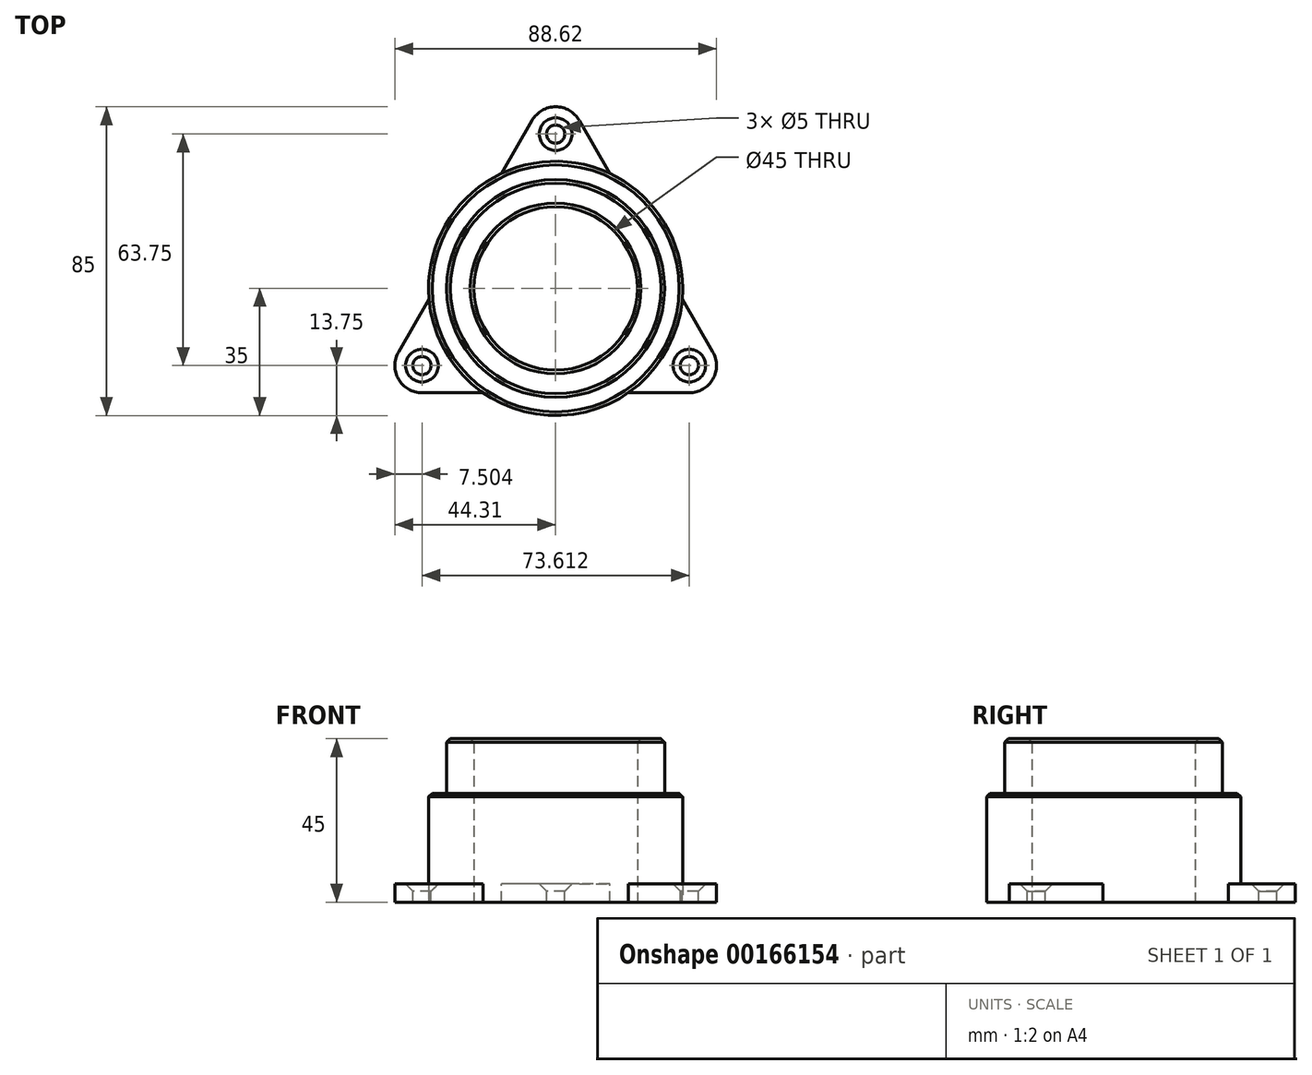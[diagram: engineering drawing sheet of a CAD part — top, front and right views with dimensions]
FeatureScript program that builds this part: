
annotation { "Feature Type Name" : "Feature", "Feature Type Description" : "" }
export const myFeature = defineFeature(function(context is Context, id is Id, definition is map)
    precondition{}
    {
        {
            var Q0;
            Q0=qCreatedBy(makeId("Top.planeOp"),FACE);
            var sketch = newSketch(context, id + "F0", { "sketchPlane" : qUnion([Q0])});
            skCircle(sketch, "E0", {"center": v(0, 0) * mm, "radius": 35 * mm});
            skArc(sketch, "E1", {"start": v(6.5, 46.25) * mm, "mid": v(0, 50) * mm, "end": v(-6.5, 46.25) * mm});
            skLineSegment(sketch, "E2", {"start": v(6.5, 46.25) * mm, "end": v(14.92, 31.66) * mm});
            skLineSegment(sketch, "E3.MirrorCS", {"start": v(-6.5, 46.25) * mm, "end": v(-14.92, 31.66) * mm});
            skCircle(sketch, "E4", {"center": v(0, 42.5) * mm, "radius": 2.5 * mm});
            skLineSegment(sketch, "E5.1.0", {"start": v(-43.3, -17.5) * mm, "end": v(-34.88, -2.91) * mm});
            skLineSegment(sketch, "E5.1.1", {"start": v(-36.8, -28.75) * mm, "end": v(-19.96, -28.75) * mm});
            skArc(sketch, "E5.1.2", {"start": v(-43.3, -17.5) * mm, "mid": v(-43.3, -25) * mm, "end": v(-36.8, -28.75) * mm});
            skCircle(sketch, "E5.1.3", {"center": v(-36.8, -21.25) * mm, "radius": 2.5 * mm});
            skLineSegment(sketch, "E5.2.0", {"start": v(36.8, -28.75) * mm, "end": v(19.96, -28.75) * mm});
            skLineSegment(sketch, "E5.2.1", {"start": v(43.3, -17.5) * mm, "end": v(34.88, -2.91) * mm});
            skArc(sketch, "E5.2.2", {"start": v(36.8, -28.75) * mm, "mid": v(43.3, -25) * mm, "end": v(43.3, -17.5) * mm});
            skCircle(sketch, "E5.2.3", {"center": v(36.8, -21.25) * mm, "radius": 2.5 * mm});
            skCircle(sketch, "E6", {"center": v(0, 0) * mm, "radius": 22.5 * mm});
            skCircle(sketch, "E7", {"center": v(0, 0) * mm, "radius": 50 * mm, "construction": true});
            skSolve(sketch);
        }
        {
            var Q0;
            {var subQ0=sQuery(id+"F0.wireOp",EDGE,"E0");var subQ5=makeQuery(id+"F0.imprint","INTERSECT",VERTEX,{"derivedFrom":[subQ0,sQuery(id+"F0.wireOp",EDGE,"E2")]});Q0=makeQuery(id+"F0.imprint","IMPRINT",FACE,{"disambiguationData":[TD([[makeQuery(id+"F0.imprint","IMPRINT",EDGE,{"disambiguationData":[TD([[subQ5,-1.0]])],"derivedFrom":subQ0}),1.0]])]});}
            extrude(context, id + "F1", {"entities" : qUnion([Q0]), "depth" : 25 * mm});
        }
        {
            var Q0;
            {var subQ1=sQuery(id+"F0.wireOp",EDGE,"E5.1.0");Q0=makeQuery(id+"F0.imprint","IMPRINT",FACE,{"disambiguationData":[TD([[makeQuery(id+"F0.imprint","IMPRINT",EDGE,{"derivedFrom":subQ1}),-1.0]])]});}
            var Q1;
            {var subQ1=sQuery(id+"F0.wireOp",EDGE,"E5.2.0");Q1=makeQuery(id+"F0.imprint","IMPRINT",FACE,{"disambiguationData":[TD([[makeQuery(id+"F0.imprint","IMPRINT",EDGE,{"derivedFrom":subQ1}),-1.0]])]});}
            var Q2;
            Q2=makeQuery(id+"F0.imprint","IMPRINT",FACE,{"disambiguationData":[TD([[makeQuery(id+"F0.imprint","IMPRINT",EDGE,{"derivedFrom":sQuery(id+"F0.wireOp",EDGE,"E1")}),1.0]])]});
            var Q3;
            {var subQ0=sQuery(id+"F0.wireOp",EDGE,"E0");var subQ5=makeQuery(id+"F0.imprint","INTERSECT",VERTEX,{"derivedFrom":[subQ0,sQuery(id+"F0.wireOp",EDGE,"E2")]});Q3=makeQuery(id+"F0.imprint","IMPRINT",FACE,{"disambiguationData":[TD([[makeQuery(id+"F0.imprint","IMPRINT",EDGE,{"disambiguationData":[TD([[subQ5,-1.0]])],"derivedFrom":subQ0}),1.0]])]});}
            extrude(context, id + "F2", {"entities" : qUnion([Q0, Q1, Q2, Q3]), "operationType" : NewBodyOperationType.ADD, "oppositeDirection" : true, "depth" : 5 * mm});
        }
        {
            var Q0;
            Q0=makeQuery(id+"F1.opExtrude","CAP_FACE",FACE,{"disambiguationData":[OSD([sQuery(id+"F0.wireOp",EDGE,"E0"),sQuery(id+"F0.wireOp",EDGE,"E6")])],"isStart":false});
            var sketch = newSketch(context, id + "F3", { "sketchPlane" : qUnion([Q0])});
            skCircle(sketch, "E8", {"center": v(0, 0) * mm, "radius": 30 * mm});
            skSolve(sketch);
        }
        {
            var Q0;
            Q0=makeQuery(id+"F3.imprint","IMPRINT",FACE,{"disambiguationData":[TD([[makeQuery(id+"F3.imprint","IMPRINT",EDGE,{"derivedFrom":sQuery(id+"F3.wireOp",EDGE,"E8")}),1.0]])]});
            extrude(context, id + "F4", {"entities" : qUnion([Q0]), "operationType" : NewBodyOperationType.ADD, "depth" : 15 * mm});
        }
        {
            var Q0;
            Q0=makeQuery(id+"F4.opExtrude","CAP_EDGE",EDGE,{"disambiguationData":[OSD([sQuery(id+"F0.wireOp",EDGE,"E6")])],"isStart":false});
            var Q1;
            Q1=makeQuery(id+"F4.opExtrude","CAP_EDGE",EDGE,{"disambiguationData":[OSD([sQuery(id+"F3.wireOp",EDGE,"E8")])],"isStart":false});
            var Q2;
            Q2=makeQuery(id+"F1.opExtrude","CAP_EDGE",EDGE,{"disambiguationData":[OSD([sQuery(id+"F0.wireOp",EDGE,"E0")])],"isStart":false});
            chamfer(context, id + "F5", {"entities" : qUnion([Q0, Q1, Q2]), "width" : 1 * mm, "tangentPropagation" : true});
        }
        {
            var Q0;
            Q0=makeQuery(id+"F2.opExtrude","CAP_EDGE",EDGE,{"disambiguationData":[OSD([sQuery(id+"F0.wireOp",EDGE,"E4")])],"isStart":true});
            var Q1;
            Q1=makeQuery(id+"F2.opExtrude","CAP_EDGE",EDGE,{"disambiguationData":[OSD([sQuery(id+"F0.wireOp",EDGE,"E5.2.3")])],"isStart":true});
            var Q2;
            Q2=makeQuery(id+"F2.opExtrude","CAP_EDGE",EDGE,{"disambiguationData":[OSD([sQuery(id+"F0.wireOp",EDGE,"E5.1.3")])],"isStart":true});
            chamfer(context, id + "F6", {"entities" : qUnion([Q0, Q1, Q2]), "width" : 2 * mm, "tangentPropagation" : true});
        }
    });
